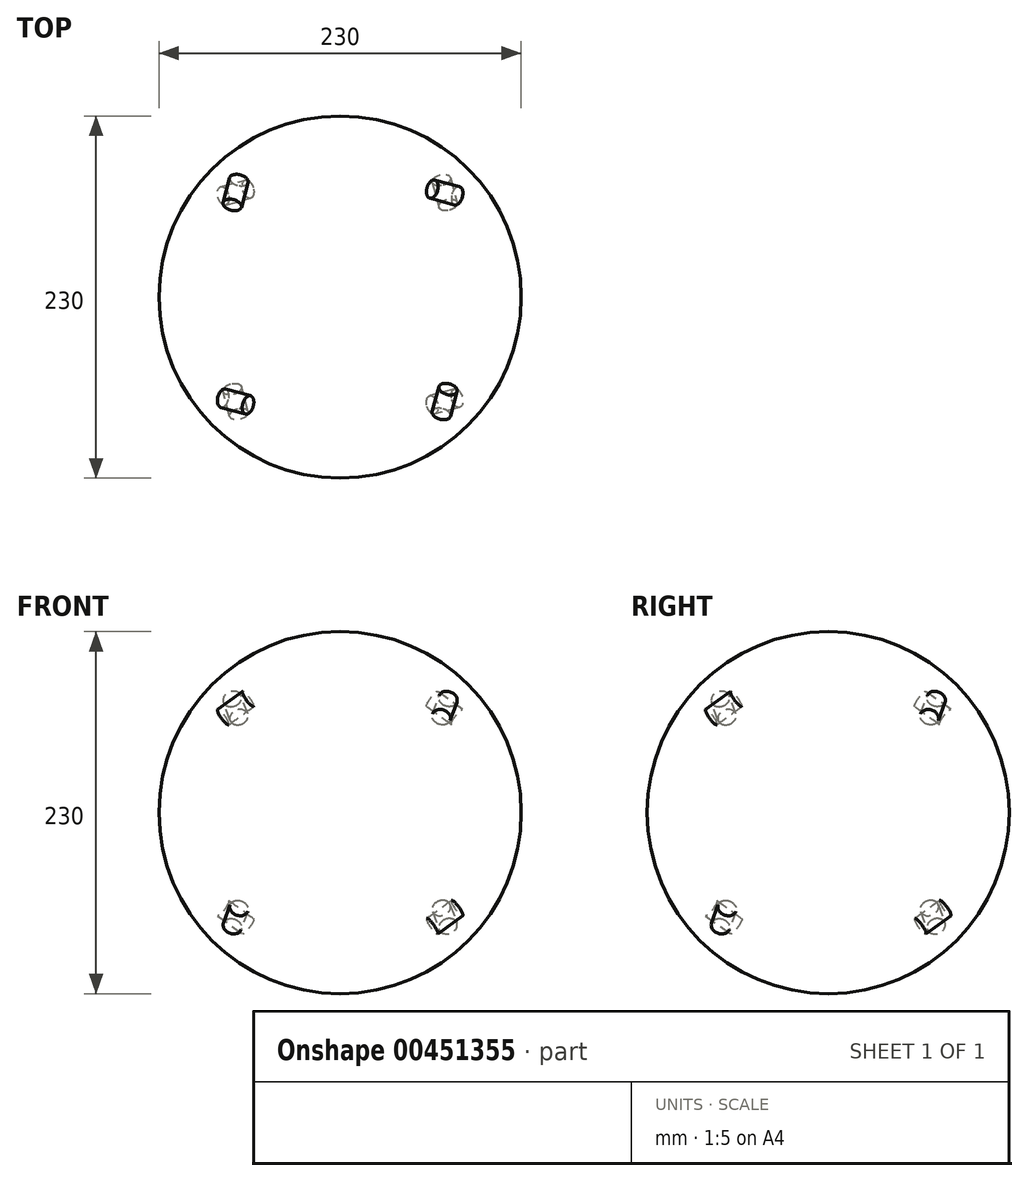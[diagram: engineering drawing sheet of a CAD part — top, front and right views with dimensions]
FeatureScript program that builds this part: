
annotation { "Feature Type Name" : "Feature", "Feature Type Description" : "" }
export const myFeature = defineFeature(function(context is Context, id is Id, definition is map)
    precondition{}
    {
        {
            var Q0;
            Q0=qCreatedBy(makeId("Top.planeOp"),FACE);
            var sketch = newSketch(context, id + "F0", { "sketchPlane" : qUnion([Q0])});
            skArc(sketch, "E0", {"start": v(115, 0) * mm, "mid": v(0, 115) * mm, "end": v(-115, 0) * mm});
            skLineSegment(sketch, "E1", {"start": v(115, 0) * mm, "end": v(-115, 0) * mm});
            skSolve(sketch);
        }
        {
            var Q0;
            Q0=makeQuery(id+"F0.imprint","IMPRINT",FACE,{"disambiguationData":[TD([[makeQuery(id+"F0.imprint","IMPRINT",EDGE,{"derivedFrom":sQuery(id+"F0.wireOp",EDGE,"E0")}),1.0]])]});
            var Q1;
            Q1=sQuery(id+"F0.wireOp",EDGE,"E1");
            revolve(context, id + "F1", {"entities" : qUnion([Q0]), "axis" : qUnion([Q1]), "revolveType" : RevolveType.FULL});
        }
        {
            var Q0;
            Q0=qCreatedBy(makeId("Front.planeOp"),FACE);
            var Q1;
            Q1=qCreatedBy(makeId("Right.planeOp"),FACE);
            cPlane(context, id + "F2", {"entities" : qUnion([Q0, Q1]), "cplaneType" : CPlaneType.MID_PLANE, "offset" : 25 * mm, "width" : 150 * mm, "height" : 150 * mm});
        }
        {
            var Q0;
            Q0=qCreatedBy(id+"F2.planeOp",FACE);
            var sketch = newSketch(context, id + "F3", { "sketchPlane" : qUnion([Q0])});
            skLineSegment(sketch, "E2", {"start": v(0, 0) * mm, "end": v(-93.9, 66.4) * mm});
            skLineSegment(sketch, "E3", {"start": v(0, 0) * mm, "end": v(-103.18, 0) * mm, "construction": true});
            skLineSegment(sketch, "E4", {"start": v(-93.9, 66.4) * mm, "end": v(-68.11, 102.86) * mm});
            skSolve(sketch);
        }
        {
            var Q0;
            Q0=sQuery(id+"F3.wireOp",VERTEX,"E2.end");
            var Q1;
            Q1=sQuery(id+"F3.wireOp",EDGE,"E2");
            cPlane(context, id + "F4", {"entities" : qUnion([Q0, Q1]), "cplaneType" : CPlaneType.LINE_POINT, "offset" : 25 * mm, "width" : 150 * mm, "height" : 150 * mm});
        }
        {
            var Q0;
            Q0=qCreatedBy(id+"F4.planeOp",FACE);
            var sketch = newSketch(context, id + "F5", { "sketchPlane" : qUnion([Q0])});
            skLineSegment(sketch, "E5.0", {"start": v(0, 0) * mm, "end": v(-29.79, 51.6) * mm});
            skLineSegment(sketch, "E6", {"start": v(2.59, 9.66) * mm, "end": v(-2.59, -9.66) * mm});
            skLineSegment(sketch, "E7", {"start": v(-2.59, -9.66) * mm, "end": v(-8.38, -8.1) * mm});
            skLineSegment(sketch, "E8", {"start": v(-8.38, -8.1) * mm, "end": v(-3.2, 11.21) * mm});
            skLineSegment(sketch, "E9", {"start": v(-3.2, 11.21) * mm, "end": v(2.59, 9.66) * mm});
            skSolve(sketch);
        }
        {
            var Q0;
            {var subQ5=sQuery(id+"F5.wireOp",EDGE,"E7");Q0=makeQuery(id+"F5.imprint","IMPRINT",FACE,{"disambiguationData":[TD([[makeQuery(id+"F5.imprint","IMPRINT",EDGE,{"derivedFrom":subQ5}),-1.0]])]});}
            var Q1;
            {var subQ5=sQuery(id+"F5.wireOp",EDGE,"E9");Q1=makeQuery(id+"F5.imprint","IMPRINT",FACE,{"disambiguationData":[TD([[makeQuery(id+"F5.imprint","IMPRINT",EDGE,{"derivedFrom":subQ5}),-1.0]])]});}
            var Q2;
            Q2=sQuery(id+"F5.wireOp",EDGE,"E6");
            revolve(context, id + "F6", {"entities" : qUnion([Q0, Q1]), "axis" : qUnion([Q2]), "revolveType" : RevolveType.FULL});
        }
        {
            var Q0;
            Q0=qCreatedBy(makeId("Front.planeOp"),FACE);
            var sketch = newSketch(context, id + "F7", { "sketchPlane" : qUnion([Q0])});
            skLineSegment(sketch, "E10", {"start": v(0, 0) * mm, "end": v(0, 99.82) * mm});
            skSolve(sketch);
        }
        {
            var Q0;
            Q0=makeQuery(id+"F6.opRevolve","SWEPT_BODY",BODY,{"disambiguationData":[OSD([sQuery(id+"F5.wireOp",EDGE,"E6"),sQuery(id+"F5.wireOp",EDGE,"E7"),sQuery(id+"F5.wireOp",EDGE,"E8"),sQuery(id+"F5.wireOp",EDGE,"E9")])]});
            var Q1;
            Q1=sQuery(id+"F7.wireOp",EDGE,"E10");
            circularPattern(context, id + "F8", {"entities" : qUnion([Q0]), "axis" : qUnion([Q1]), "angle" : 360 * degree, "instanceCount" : 4, "equalSpace" : true});
        }
        {
            var Q0;
            Q0=makeQuery(id+"F8.opPattern","COPY",BODY,{"derivedFrom":makeQuery(id+"F6.opRevolve","SWEPT_BODY",BODY,{"disambiguationData":[OSD([sQuery(id+"F5.wireOp",EDGE,"E6"),sQuery(id+"F5.wireOp",EDGE,"E7"),sQuery(id+"F5.wireOp",EDGE,"E8"),sQuery(id+"F5.wireOp",EDGE,"E9")])]}),"instanceName":"3"});
            var Q1;
            Q1=makeQuery(id+"F6.opRevolve","SWEPT_BODY",BODY,{"disambiguationData":[OSD([sQuery(id+"F5.wireOp",EDGE,"E6"),sQuery(id+"F5.wireOp",EDGE,"E7"),sQuery(id+"F5.wireOp",EDGE,"E8"),sQuery(id+"F5.wireOp",EDGE,"E9")])]});
            var Q2;
            Q2=makeQuery(id+"F8.opPattern","COPY",BODY,{"derivedFrom":makeQuery(id+"F6.opRevolve","SWEPT_BODY",BODY,{"disambiguationData":[OSD([sQuery(id+"F5.wireOp",EDGE,"E6"),sQuery(id+"F5.wireOp",EDGE,"E7"),sQuery(id+"F5.wireOp",EDGE,"E8"),sQuery(id+"F5.wireOp",EDGE,"E9")])]}),"instanceName":"2"});
            var Q3;
            Q3=makeQuery(id+"F8.opPattern","COPY",BODY,{"derivedFrom":makeQuery(id+"F6.opRevolve","SWEPT_BODY",BODY,{"disambiguationData":[OSD([sQuery(id+"F5.wireOp",EDGE,"E6"),sQuery(id+"F5.wireOp",EDGE,"E7"),sQuery(id+"F5.wireOp",EDGE,"E8"),sQuery(id+"F5.wireOp",EDGE,"E9")])]}),"instanceName":"1"});
            var Q4;
            Q4=sQuery(id+"F0.wireOp",EDGE,"E1");
            circularPattern(context, id + "F9", {"entities" : qUnion([Q0, Q1, Q2, Q3]), "axis" : qUnion([Q4]), "angle" : 360 * degree, "instanceCount" : 2, "equalSpace" : true});
        }
    });
